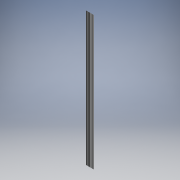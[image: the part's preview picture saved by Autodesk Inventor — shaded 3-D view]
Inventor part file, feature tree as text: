
AUTODESK INVENTOR PART (.ipt)
format: ipt  version: 2017.3 (Build 213256000, 256)  size: 258,048 bytes
history: native  units: mm (DEFAULTED — no unit token found)
features: other x21, sketch x5, extrude x3, hole x2, pattern_linear x1
ambient origin geometry x8: Origin, YZ Plane, XZ Plane, XY Plane, X Axis, Y Axis, Z Axis, Center Point
bodies: Solid1 (feature_tree)
feature tree (32):
  extrude  "Extrusion1"  Depth=2.0mm
  hole  "Hole1"  [1 undecoded]
  hole  "Hole2"  [1 undecoded]
  pattern_linear  "Rectangular Pattern1"  [2 undecoded]
  extrude  "Extrusion2"  [1 undecoded]
  extrude  "Extrusion3"  [1 undecoded]
  other  "C1_XY"
  other  "C1_YZ"
  other  "C1_ZX"
  other  "C1_X"
  other  "C1_Y"
  other  "C1_Z"
  other  "C1_Center"
  other  "to_frame_cap1_XY"
  other  "to_frame_cap1_YZ"
  other  "to_frame_cap1_ZX"
  other  "to_frame_cap1_X"
  other  "to_frame_cap1_Y"
  other  "to_frame_cap1_Z"
  other  "to_frame_cap1_Center"
  other  "to_frame_cap2_XY"
  other  "to_frame_cap2_YZ"
  other  "to_frame_cap2_ZX"
  other  "to_frame_cap2_X"
  other  "to_frame_cap2_Y"
  other  "to_frame_cap2_Z"
  other  "to_frame_cap2_Center"
  sketch  "Sketch_1"  dims[d0=1005.5mm d1=0.0mm]
  sketch  "Sketch2"  dims[d2=6.8mm d3=6.0mm d4=4.0mm d5=2.0mm d6=90.0deg d7=1005.5mm d8=0.0mm]
  sketch  "Sketch3"  dims[d9=4.2mm d10=6.0mm d11=4.0mm d12=2.0mm d13=90.0deg d14=1005.5mm d15=0.0mm d16=20.0mm d18=23.2mm d19=20.0mm d21=23.2mm]
  sketch  "Sketch_5"  dims[d22=30.0mm d23=0.0mm d24=30.0mm d25=0.0mm]
  sketch  "Sketch_8"
note: 6 required parameter values undecoded (feature->parameter linkage not recoverable at this tier; creation-order binding heuristic only, values carry confidence <= 0.55)
